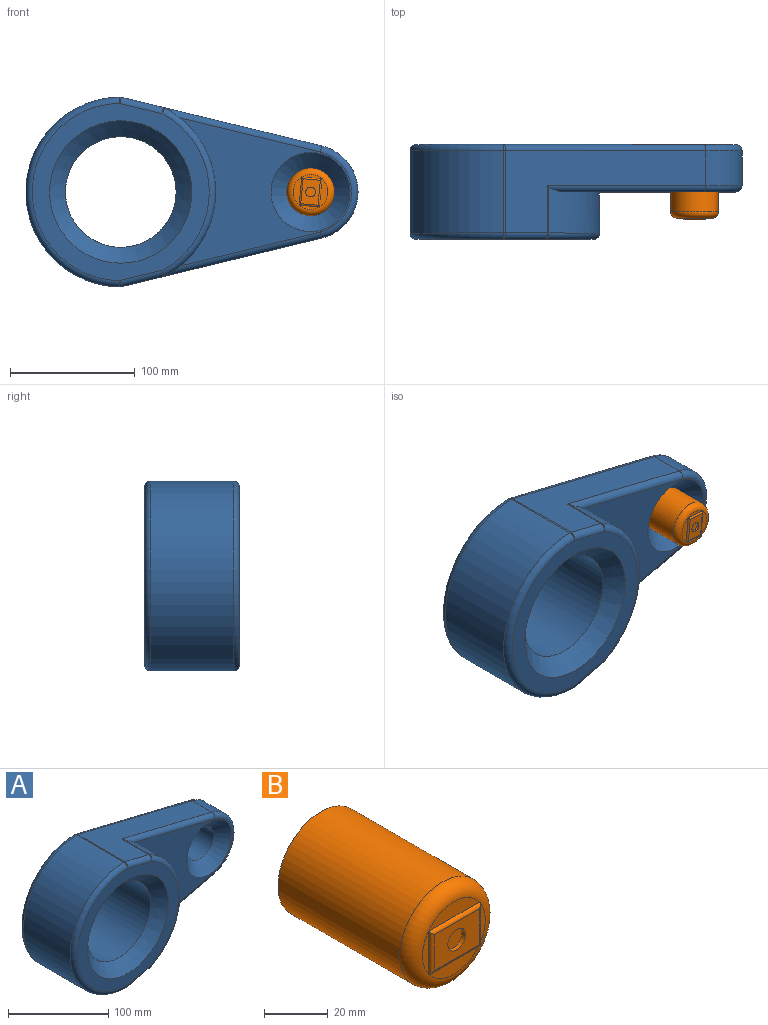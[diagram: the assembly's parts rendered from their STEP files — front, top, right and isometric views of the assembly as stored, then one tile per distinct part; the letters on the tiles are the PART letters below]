
ASSEMBLY  parts=2 mates=1
PART A: 33 faces, bbox 276.1x76.2x165 mm
  f0: torus R=71.12mm, axis (0,-1,0), area 1288.8mm2, adj f9,f10,f18,f32
  f1: plane 137.67x118.76mm, normal (0,-1,0), area 5968.1mm2, adj f9,f12,f13,f14,f15
  f2: plane 160.79x66.04mm, normal (0.24,0,-0.97), area 5945.4mm2, adj f3,f14,f25,f28,f30,f31
  f3: cylinder r=38.1mm len=74.05mm, axis (0,1,0), area 2837.3mm2, adj f2,f4,f13,f23
  f4: plane 160.79x66.04mm, normal (0.24,0,0.97), area 5945.4mm2, adj f3,f12,f17,f19,f21,f22
  f5: cylinder r=76.2mm len=152.39mm, axis (0,1,0), area 15724.7mm2, adj f11,f22,f26,f28
  f6: cylinder r=44.45mm len=88.9mm, axis (0,1,0), area 17734.8mm2, adj f8,f16
  f7: cylinder r=19.05mm len=38.1mm, axis (0,1,0), area 3040.2mm2, adj f8,f15
  f8: plane 256.54x142.24mm, normal (0,1,0), area 18310.1mm2, adj f6,f7,f21,f23,f25,f26
  f9: cylinder r=76.2mm len=134.85mm, axis (0,1,0), area 5499.4mm2, adj f0,f1,f12,f14,f17,f30
  f10: plane 142.24x142.24mm, normal (0,-1,0), area 5529.7mm2, adj f0,f11,f16,f19,f31
  f11: torus R=71.12mm, axis (0,-1,0), area 1854mm2, adj f5,f10,f20,f29
  f12: cylinder r=5.08mm len=128.25mm, axis (0.97,0,-0.24), area 991.6mm2, adj f1,f4,f9,f13,f17
  f13: torus R=33.02mm, axis (0,-1,0), area 771.1mm2, adj f1,f3,f12,f14
  f14: cylinder r=5.08mm len=128.25mm, axis (-0.97,0,-0.24), area 991.6mm2, adj f1,f2,f9,f13,f30
  f15: cone r=19.05mm half-angle=45deg, axis (0,-1,0), area 2866.4mm2, adj f1,f7
  f16: cone r=44.45mm half-angle=45deg, axis (0,-1,0), area 5732.7mm2, adj f6,f10
  f17: cylinder r=5.08mm len=38.1mm, axis (0,1,0), area 46.9mm2, adj f4,f9,f12,f18
  f18: sphere r=5.08mm, area 6.4mm2, adj f0,f17,f19
  f19: cylinder r=5.08mm len=34.93mm, axis (0.97,0,-0.24), area 277mm2, adj f4,f10,f18,f20
  f20: sphere r=5.08mm, area 6.4mm2, adj f11,f19,f22
  f21: cylinder r=5.08mm len=161.99mm, axis (-0.97,0,0.24), area 1320.3mm2, adj f4,f8,f23,f24
  f22: cylinder r=5.08mm len=66.04mm, axis (0,1,0), area 82.7mm2, adj f4,f5,f20,f24
  f23: torus R=33.02mm, axis (0,-1,0), area 771.1mm2, adj f3,f8,f21,f25
  f24: sphere r=5.08mm, area 6.4mm2, adj f21,f22,f26
  f25: cylinder r=5.08mm len=161.99mm, axis (0.97,0,0.24), area 1320.3mm2, adj f2,f8,f23,f27
  f26: torus R=71.12mm, axis (0,-1,0), area 1854mm2, adj f5,f8,f24,f27
  f27: sphere r=5.08mm, area 6.4mm2, adj f25,f26,f28
  f28: cylinder r=5.08mm len=66.04mm, axis (0,1,0), area 82.7mm2, adj f2,f5,f27,f29
  f29: sphere r=5.08mm, area 6.4mm2, adj f11,f28,f31
  f30: cylinder r=5.08mm len=38.1mm, axis (0,1,0), area 46.9mm2, adj f2,f9,f14,f32
  f31: cylinder r=5.08mm len=34.93mm, axis (0.97,0,0.24), area 277mm2, adj f2,f10,f29,f32
  f32: sphere r=5.08mm, area 6.4mm2, adj f0,f30,f31
PART B: 14 faces, bbox 41.2x60.5x41.2 mm
  f0: plane 22.64x5.78mm, normal (0,-1,0), area 91.6mm2, adj f6,f8
  f1: plane 16.38x2.65mm, normal (0,-1,0), area 29.6mm2, adj f6,f10
  f2: plane 22.64x5.78mm, normal (0,-1,0), area 91.6mm2, adj f6,f11
  f3: cylinder r=19.05mm len=54.1mm, axis (0,1,0), area 6475.7mm2, adj f5,f6
  f4: plane 16.38x2.65mm, normal (0,-1,0), area 29.6mm2, adj f6,f9
  f5: plane 38.1x38.1mm, normal (0,1,0), area 1140.1mm2, adj f3
  f6: torus R=13.97mm, axis (0,-1,0), area 862.6mm2, adj f0,f1,f2,f3,f4
  f7: plane 20.1x13.84mm, normal (0,-1,0), area 229.5mm2, adj f8,f9,f10,f11,f12
  f8: cylinder r=1.27mm len=22.64mm, axis (-1,0,0), area 43.3mm2, adj f0,f7,f9,f10
  f9: cylinder r=1.27mm len=16.38mm, axis (0,0,-1), area 30.8mm2, adj f4,f7,f8,f11
  f10: cylinder r=1.27mm len=16.38mm, axis (0,0,1), area 30.8mm2, adj f1,f7,f8,f11
  f11: cylinder r=1.27mm len=22.64mm, axis (1,0,0), area 43.3mm2, adj f2,f7,f9,f10
  f12: cylinder r=3.94mm len=7.87mm, axis (0,-1,0), area 39.6mm2, adj f7,f13
  f13: plane 7.87x7.87mm, normal (0,-1,0), area 48.6mm2, adj f12
PLACE A t=(-4.78,95.67,41.01)mm fixed
PLACE B rot(axis=(0,-1,0),84.5deg) t=(147.62,95.67,41.01)mm
MATE cylindrical B.f3 <-> A.f3  axis (0,1,0) through (147.62,95.67,41.01)mm
